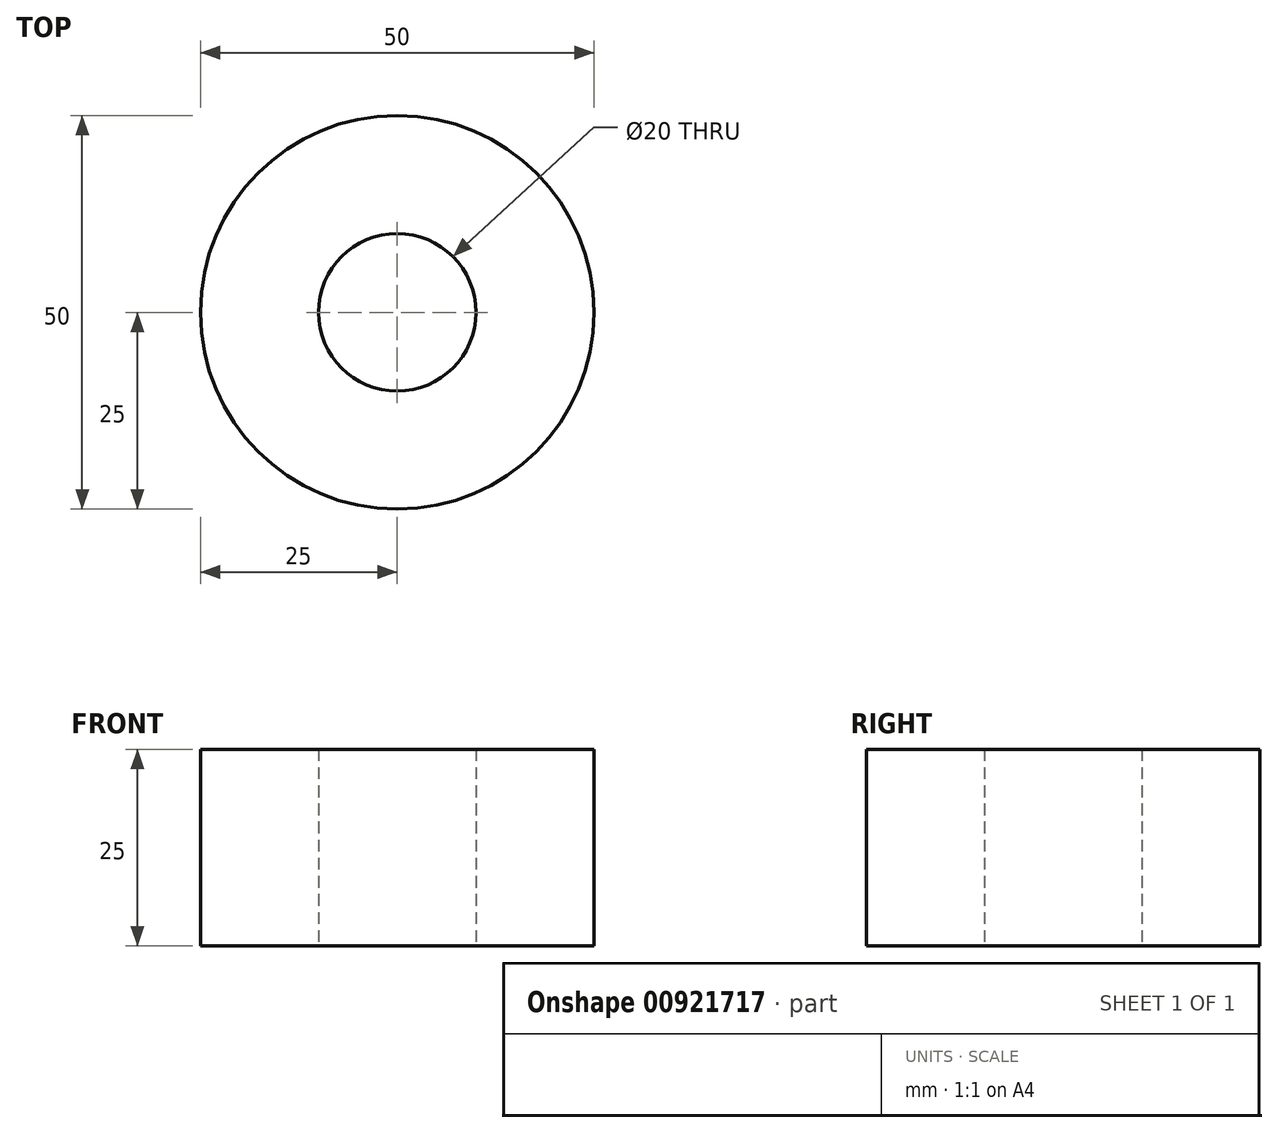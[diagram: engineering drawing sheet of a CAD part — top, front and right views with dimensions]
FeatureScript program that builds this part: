
annotation { "Feature Type Name" : "Feature", "Feature Type Description" : "" }
export const myFeature = defineFeature(function(context is Context, id is Id, definition is map)
    precondition{}
    {
        {
            var Q0;
            Q0=qCreatedBy(makeId("Top.planeOp"),FACE);
            var sketch = newSketch(context, id + "F0", { "sketchPlane" : qUnion([Q0])});
            skCircle(sketch, "E0", {"center": v(0, 0) * mm, "radius": 25 * mm});
            skCircle(sketch, "E1", {"center": v(0, 0) * mm, "radius": 10 * mm});
            skSolve(sketch);
        }
        {
            var Q0;
            Q0=makeQuery(id+"F0.imprint","IMPRINT",FACE,{"disambiguationData":[TD([[makeQuery(id+"F0.imprint","IMPRINT",EDGE,{"derivedFrom":sQuery(id+"F0.wireOp",EDGE,"E0")}),1.0]])]});
            extrude(context, id + "F1", {"entities" : qUnion([Q0]), "depth" : 25 * mm, "offsetDistance" : 25 * mm});
        }
    });
